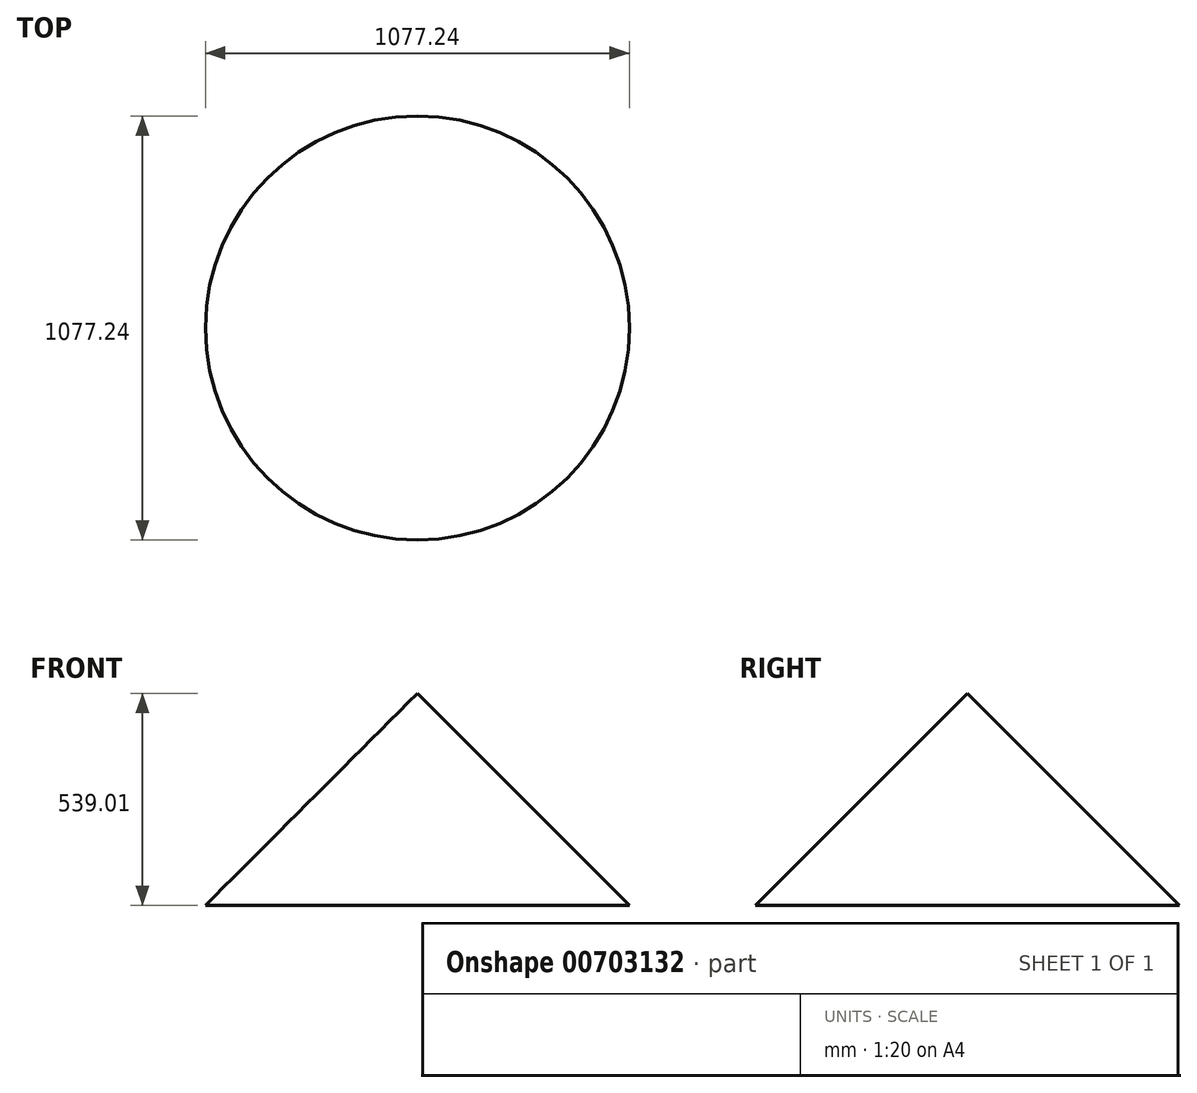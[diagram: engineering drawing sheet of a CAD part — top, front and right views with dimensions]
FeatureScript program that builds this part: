
annotation { "Feature Type Name" : "Feature", "Feature Type Description" : "" }
export const myFeature = defineFeature(function(context is Context, id is Id, definition is map)
    precondition{}
    {
        {
            var Q0;
            Q0=qCreatedBy(makeId("Front.planeOp"),FACE);
            var sketch = newSketch(context, id + "F0", { "sketchPlane" : qUnion([Q0])});
            skLineSegment(sketch, "E0.bottom", {"start": v(0, 0) * mm, "end": v(-538.62, -1.67) * mm});
            skLineSegment(sketch, "E0.left", {"start": v(0, 0) * mm, "end": v(0, 537.34) * mm});
            skLineSegment(sketch, "E1", {"start": v(-538.62, -1.67) * mm, "end": v(0, 537.34) * mm});
            skSolve(sketch);
        }
        {
            var Q0;
            Q0=makeQuery(id+"F0.imprint","IMPRINT",FACE,{"disambiguationData":[TD([[makeQuery(id+"F0.imprint","IMPRINT",EDGE,{"derivedFrom":sQuery(id+"F0.wireOp",EDGE,"E0.bottom")}),-1.0]])]});
            var Q1;
            Q1=sQuery(id+"F0.wireOp",EDGE,"E0.left");
            revolve(context, id + "F1", {"surfaceOperationType" : NewSurfaceOperationType.NEW, "entities" : qUnion([Q0]), "axis" : qUnion([Q1]), "revolveType" : RevolveType.FULL});
        }
    });
